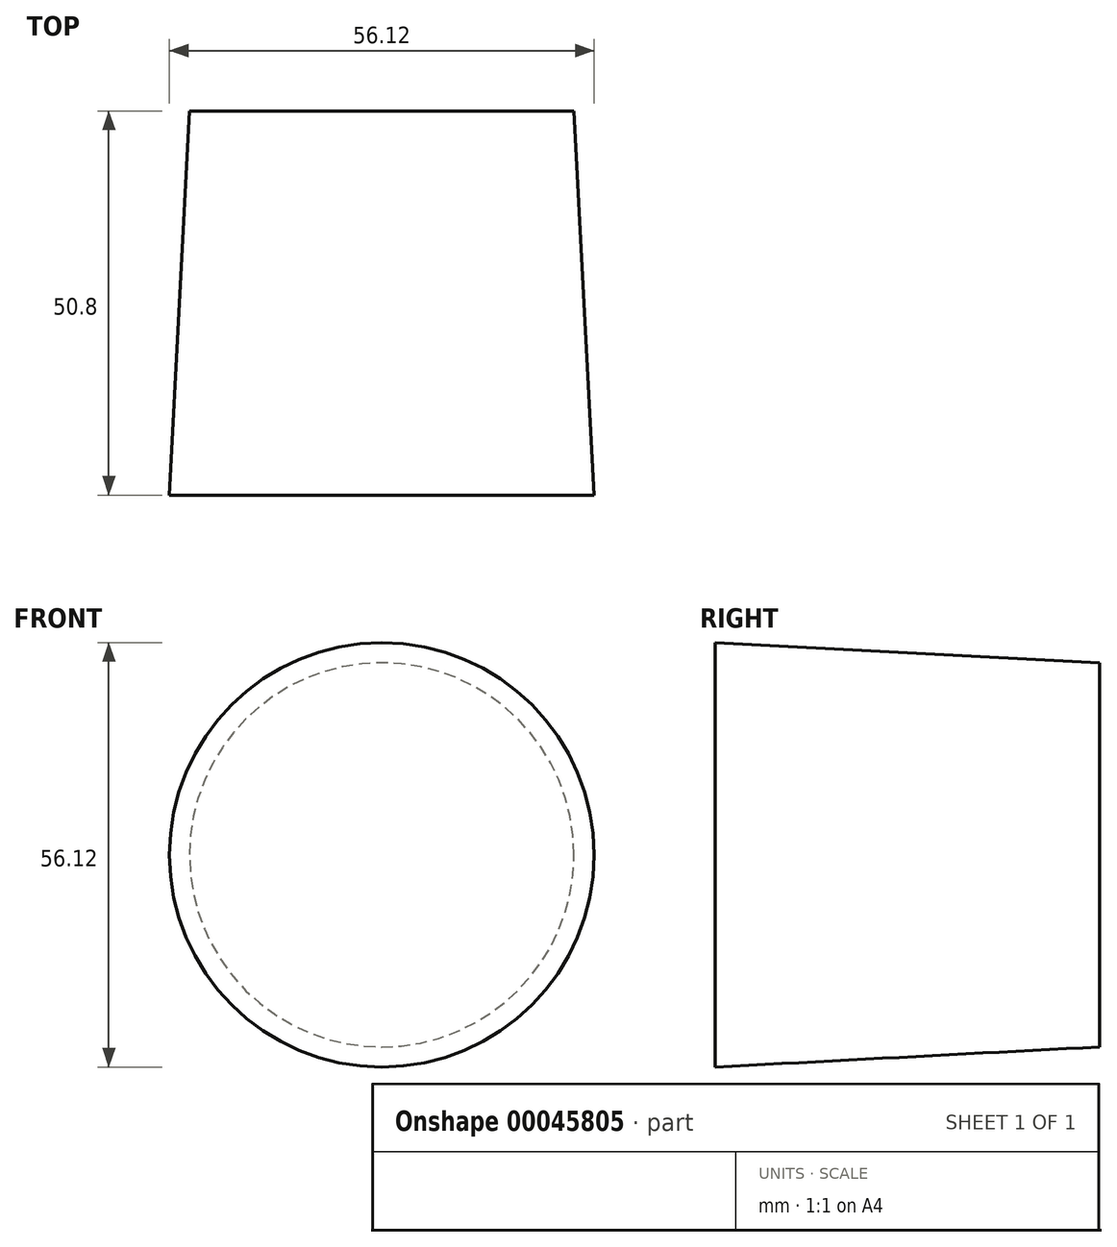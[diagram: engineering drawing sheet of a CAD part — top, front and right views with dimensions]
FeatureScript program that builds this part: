
annotation { "Feature Type Name" : "Feature", "Feature Type Description" : "" }
export const myFeature = defineFeature(function(context is Context, id is Id, definition is map)
    precondition{}
    {
        {
            var Q0;
            Q0=qCreatedBy(makeId("Front.planeOp"),FACE);
            var sketch = newSketch(context, id + "F1", { "sketchPlane" : qUnion([Q0])});
            skCircle(sketch, "E0", {"center": v(0, 0) * mm, "radius": 25.4 * mm});
            skSolve(sketch);
        }
        {
            var Q0;
            Q0 = qSketchRegion(id + "F1", true);
            extrude(context, id + "F0", {"entities" : qUnion([Q0]), "depth" : 50.8 * mm, "hasDraft" : true, "draftAngle" : 3 * degree});
        }
    });
